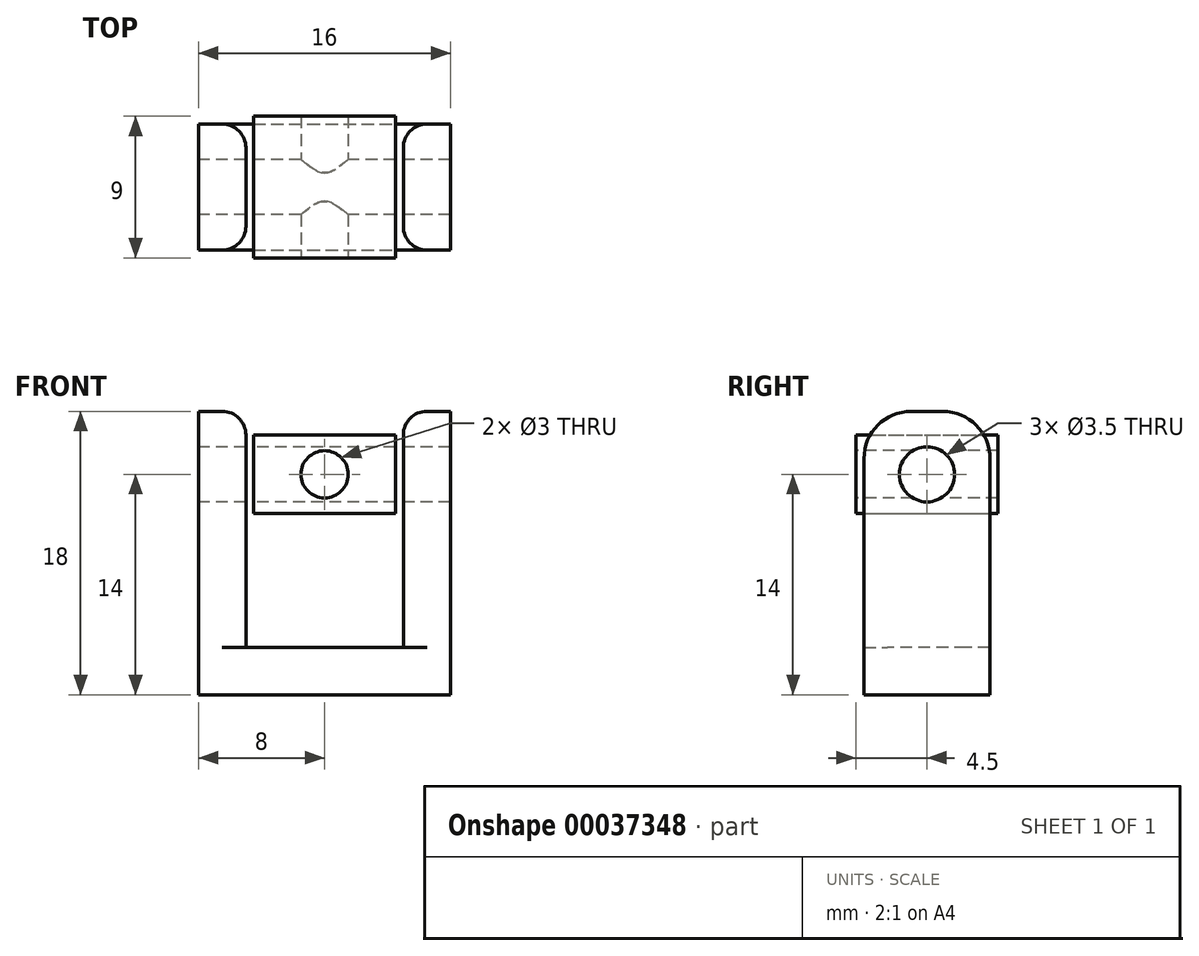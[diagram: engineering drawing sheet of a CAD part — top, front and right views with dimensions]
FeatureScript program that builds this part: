
annotation { "Feature Type Name" : "Feature", "Feature Type Description" : "" }
export const myFeature = defineFeature(function(context is Context, id is Id, definition is map)
    precondition{}
    {
        {
            var Q0;
            Q0=qCreatedBy(makeId("Top.planeOp"),FACE);
            var sketch = newSketch(context, id + "F0", { "sketchPlane" : qUnion([Q0])});
            skLineSegment(sketch, "E0.bottom", {"start": v(-8, 4) * mm, "end": v(8, 4) * mm});
            skLineSegment(sketch, "E0.top", {"start": v(-8, -4) * mm, "end": v(8, -4) * mm});
            skLineSegment(sketch, "E0.left", {"start": v(-8, 4) * mm, "end": v(-8, -4) * mm});
            skLineSegment(sketch, "E0.right", {"start": v(8, 4) * mm, "end": v(8, -4) * mm});
            skLineSegment(sketch, "E1", {"start": v(-8, 0) * mm, "end": v(8, 0) * mm});
            skSolve(sketch);
        }
        {
            var Q0;
            Q0=qSketchRegion(id+"F0",true);
            extrude(context, id + "F1", {"entities" : qUnion([Q0]), "depth" : 3 * mm});
        }
        {
            var Q0;
            Q0=makeQuery(id+"F1.opExtrude","CAP_FACE",FACE,{"disambiguationData":[OSD([sQuery(id+"F0.wireOp",EDGE,"E0.bottom"),sQuery(id+"F0.wireOp",EDGE,"E0.top"),sQuery(id+"F0.wireOp",EDGE,"E0.left"),sQuery(id+"F0.wireOp",EDGE,"E0.right")])],"isStart":false});
            var sketch = newSketch(context, id + "F2", { "sketchPlane" : qUnion([Q0])});
            skLineSegment(sketch, "E2.bottom", {"start": v(-8, 4) * mm, "end": v(-5, 4) * mm});
            skLineSegment(sketch, "E2.top", {"start": v(-8, -4) * mm, "end": v(-5, -4) * mm});
            skLineSegment(sketch, "E2.left", {"start": v(-8, 4) * mm, "end": v(-8, -4) * mm});
            skLineSegment(sketch, "E2.right", {"start": v(-5, 4) * mm, "end": v(-5, -4) * mm});
            skLineSegment(sketch, "E3", {"start": v(0, -4) * mm, "end": v(0, 4) * mm});
            skLineSegment(sketch, "E4.0.MirrorCS", {"start": v(5, 4) * mm, "end": v(5, -4) * mm});
            skLineSegment(sketch, "E4.1.MirrorCS", {"start": v(8, 4) * mm, "end": v(8, -4) * mm});
            skLineSegment(sketch, "E4.2.MirrorCS", {"start": v(8, -4) * mm, "end": v(5, -4) * mm});
            skLineSegment(sketch, "E4.3.MirrorCS", {"start": v(8, 4) * mm, "end": v(5, 4) * mm});
            skLineSegment(sketch, "E5", {"start": v(0, 0) * mm, "end": v(-5, 0) * mm});
            skSolve(sketch);
        }
        {
            var Q0;
            Q0=qSketchRegion(id+"F2",true);
            extrude(context, id + "F3", {"entities" : qUnion([Q0]), "operationType" : NewBodyOperationType.ADD, "depth" : 15 * mm});
        }
        {
            var Q0;
            Q0=makeQuery(id+"F3.opExtrude","SWEPT_FACE",FACE,{"disambiguationData":[OSD([sQuery(id+"F2.wireOp",EDGE,"E2.right")])]});
            var sketch = newSketch(context, id + "F4", { "sketchPlane" : qUnion([Q0])});
            skLineSegment(sketch, "E6", {"start": v(4, 9) * mm, "end": v(-4, 9) * mm});
            skSolve(sketch);
        }
        {
            var Q0;
            {var subQ2=sQuery(id+"F4.wireOp",EDGE,"E6");Q0=makeQuery(id+"F4.imprint","IMPRINT",FACE,{"disambiguationData":[TD([[makeQuery(id+"F4.imprint","IMPRINT",EDGE,{"derivedFrom":subQ2}),-1.0]])]});}
            var sketch = newSketch(context, id + "F5", { "sketchPlane" : qUnion([Q0])});
            skLineSegment(sketch, "E7", {"start": v(-4, 14) * mm, "end": v(4, 14) * mm});
            skLineSegment(sketch, "E8", {"start": v(0, 18) * mm, "end": v(0, 14) * mm});
            skLineSegment(sketch, "E9", {"start": v(0, 14) * mm, "end": v(4, 14) * mm});
            skSolve(sketch);
        }
        {
            var Q0;
            Q0=qCreatedBy(makeId("Top.planeOp"),FACE);
            var Q1;
            Q1=sQuery(id+"F5.wireOp",VERTEX,"E9.start");
            cPlane(context, id + "F6", {"entities" : qUnion([Q0, Q1]), "cplaneType" : CPlaneType.PLANE_POINT, "offset" : 150 * mm, "width" : 150 * mm, "height" : 150 * mm});
        }
        {
            var Q0;
            Q0=qCreatedBy(id+"F6.planeOp",FACE);
            var sketch = newSketch(context, id + "F7", { "sketchPlane" : qUnion([Q0])});
            skLineSegment(sketch, "E10.rect.bottom", {"start": v(-4.5, -4.5) * mm, "end": v(4.5, -4.5) * mm});
            skLineSegment(sketch, "E10.rect.top", {"start": v(-4.5, 4.5) * mm, "end": v(4.5, 4.5) * mm});
            skLineSegment(sketch, "E10.rect.left", {"start": v(-4.5, -4.5) * mm, "end": v(-4.5, 4.5) * mm});
            skLineSegment(sketch, "E10.rect.right", {"start": v(4.5, -4.5) * mm, "end": v(4.5, 4.5) * mm});
            skPoint(sketch, "E10.rect.middle", {"position": v(0, 0) * mm});
            skSolve(sketch);
        }
        {
            var Q0;
            Q0=makeQuery(id+"F3.opExtrude","CAP_EDGE",EDGE,{"disambiguationData":[OSD([sQuery(id+"F2.wireOp",EDGE,"E2.bottom")])],"isStart":false});
            var Q1;
            Q1=makeQuery(id+"F3.opExtrude","CAP_EDGE",EDGE,{"disambiguationData":[OSD([sQuery(id+"F2.wireOp",EDGE,"E2.top")])],"isStart":false});
            var Q2;
            Q2=makeQuery(id+"F3.opExtrude","CAP_EDGE",EDGE,{"disambiguationData":[OSD([sQuery(id+"F2.wireOp",EDGE,"E4.2.MirrorCS")])],"isStart":false});
            var Q3;
            Q3=makeQuery(id+"F3.opExtrude","CAP_EDGE",EDGE,{"disambiguationData":[OSD([sQuery(id+"F2.wireOp",EDGE,"E4.3.MirrorCS")])],"isStart":false});
            fillet(context, id + "F8", {"entities" : qUnion([Q0, Q1, Q2, Q3]), "radius" : 3 * mm, "tangentPropagation" : true, "allowEdgeOverflow" : false});
        }
        {
            var Q0;
            Q0=qSketchRegion(id+"F7",true);
            extrude(context, id + "F9", {"entities" : qUnion([Q0]), "endBound" : BoundingType.SYMMETRIC, "depth" : 5 * mm});
        }
        {
            var Q0;
            Q0=makeQuery(id+"F9.opExtrude","SWEPT_FACE",FACE,{"disambiguationData":[OSD([sQuery(id+"F7.wireOp",EDGE,"E10.rect.bottom")])]});
            var sketch = newSketch(context, id + "F10", { "sketchPlane" : qUnion([Q0])});
            skCircle(sketch, "E11", {"center": v(0, 14) * mm, "radius": 1.5 * mm});
            skLineSegment(sketch, "E12", {"start": v(0, 12.5) * mm, "end": v(0, 15.5) * mm});
            skLineSegment(sketch, "E13", {"start": v(0, 16.5) * mm, "end": v(0, 11.5) * mm});
            skSolve(sketch);
        }
        {
            var Q0;
            Q0=qSketchRegion(id+"F10",true);
            var Q1;
            Q1=makeQuery(id+"F9.opExtrude","SWEPT_FACE",FACE,{"disambiguationData":[OSD([sQuery(id+"F7.wireOp",EDGE,"E10.rect.top")])]});
            extrude(context, id + "F11", {"entities" : qUnion([Q0]), "operationType" : NewBodyOperationType.REMOVE, "endBound" : BoundingType.UP_TO_SURFACE, "oppositeDirection" : true, "endBoundEntityFace" : qUnion([Q1]), "depth" : 25 * mm});
        }
        {
            var Q0;
            Q0=makeQuery(id+"F9.opExtrude","SWEPT_FACE",FACE,{"disambiguationData":[OSD([sQuery(id+"F7.wireOp",EDGE,"E10.rect.right")])]});
            var sketch = newSketch(context, id + "F12", { "sketchPlane" : qUnion([Q0])});
            skCircle(sketch, "E14", {"center": v(0, 14) * mm, "radius": 1.5 * mm});
            skLineSegment(sketch, "E15", {"start": v(0, 12.5) * mm, "end": v(0, 15.5) * mm});
            skLineSegment(sketch, "E16", {"start": v(0, 16.5) * mm, "end": v(0, 11.5) * mm});
            skSolve(sketch);
        }
        {
            var Q0;
            Q0=qSketchRegion(id+"F12",true);
            var Q1;
            Q1=makeQuery(id+"F9.opExtrude","SWEPT_FACE",FACE,{"disambiguationData":[OSD([sQuery(id+"F7.wireOp",EDGE,"E10.rect.left")])]});
            extrude(context, id + "F13", {"entities" : qUnion([Q0]), "operationType" : NewBodyOperationType.REMOVE, "endBound" : BoundingType.UP_TO_SURFACE, "oppositeDirection" : true, "endBoundEntityFace" : qUnion([Q1]), "depth" : 25 * mm});
        }
        {
            var Q0;
            Q0=makeQuery(id+"F3.boolean.opBoolean","MERGE",FACE,{"derivedFrom":[makeQuery(id+"F1.opExtrude","SWEPT_FACE",FACE,{"disambiguationData":[OSD([sQuery(id+"F0.wireOp",EDGE,"E0.left")])]}),makeQuery(id+"F3.opExtrude","SWEPT_FACE",FACE,{"disambiguationData":[OSD([sQuery(id+"F2.wireOp",EDGE,"E2.left")])]})]});
            var sketch = newSketch(context, id + "F14", { "sketchPlane" : qUnion([Q0])});
            skCircle(sketch, "E17", {"center": v(0, 14) * mm, "radius": 1.75 * mm});
            skLineSegment(sketch, "E18", {"start": v(0, 15.75) * mm, "end": v(0, 12.25) * mm});
            skSolve(sketch);
        }
        {
            var Q0;
            Q0=qSketchRegion(id+"F14",true);
            var Q1;
            Q1=makeQuery(id+"F3.boolean.opBoolean","MERGE",FACE,{"derivedFrom":[makeQuery(id+"F1.opExtrude","SWEPT_FACE",FACE,{"disambiguationData":[OSD([sQuery(id+"F0.wireOp",EDGE,"E0.right")])]}),makeQuery(id+"F3.opExtrude","SWEPT_FACE",FACE,{"disambiguationData":[OSD([sQuery(id+"F2.wireOp",EDGE,"E4.1.MirrorCS")])]})]});
            extrude(context, id + "F15", {"entities" : qUnion([Q0]), "operationType" : NewBodyOperationType.REMOVE, "endBound" : BoundingType.UP_TO_SURFACE, "oppositeDirection" : true, "endBoundEntityFace" : qUnion([Q1]), "depth" : 25 * mm});
        }
        {
            var Q0;
            Q0=makeQuery(id+"F3.opExtrude","CAP_EDGE",EDGE,{"disambiguationData":[OSD([sQuery(id+"F2.wireOp",EDGE,"E2.right")])],"isStart":false});
            var Q1;
            Q1=makeQuery(id+"F3.opExtrude","CAP_EDGE",EDGE,{"disambiguationData":[OSD([sQuery(id+"F2.wireOp",EDGE,"E4.0.MirrorCS")])],"isStart":false});
            fillet(context, id + "F16", {"entities" : qUnion([Q0, Q1]), "radius" : 1.5 * mm, "tangentPropagation" : true, "allowEdgeOverflow" : false});
        }
    });
